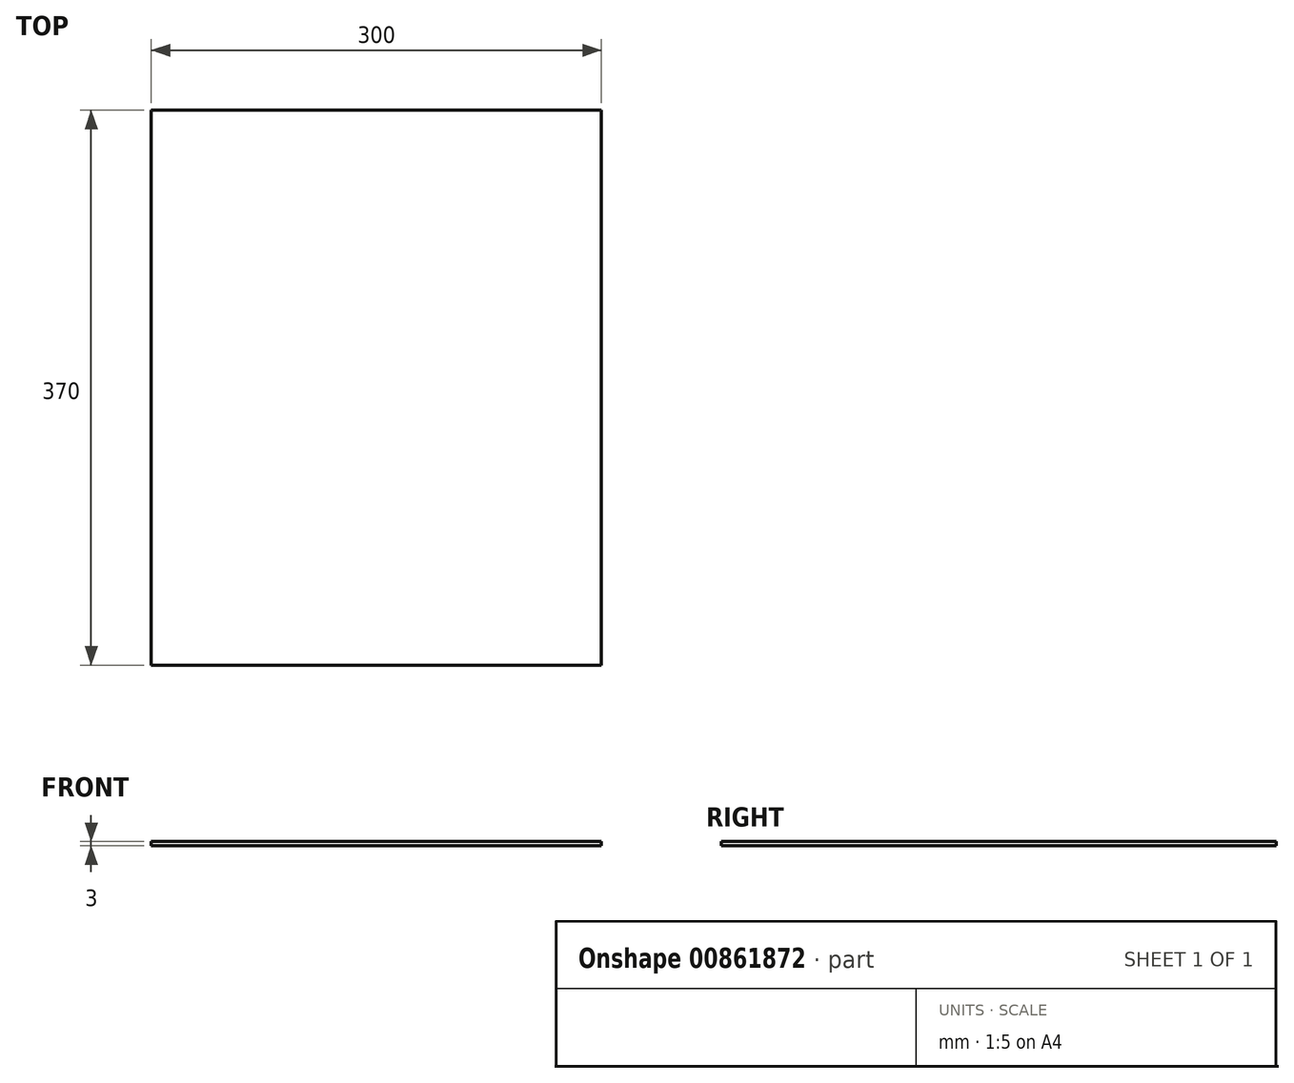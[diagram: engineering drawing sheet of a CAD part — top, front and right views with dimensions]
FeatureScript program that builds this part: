
annotation { "Feature Type Name" : "Feature", "Feature Type Description" : "" }
export const myFeature = defineFeature(function(context is Context, id is Id, definition is map)
    precondition{}
    {
        {
            var Q0;
            Q0=qCreatedBy(makeId("Top.planeOp"),FACE);
            var sketch = newSketch(context, id + "F0", { "sketchPlane" : qUnion([Q0])});
            skLineSegment(sketch, "E0.bottom", {"start": v(150, -185) * mm, "end": v(-150, -185) * mm});
            skLineSegment(sketch, "E0.top", {"start": v(150, 185) * mm, "end": v(-150, 185) * mm});
            skLineSegment(sketch, "E0.left", {"start": v(150, -185) * mm, "end": v(150, 185) * mm});
            skLineSegment(sketch, "E0.right", {"start": v(-150, -185) * mm, "end": v(-150, 185) * mm});
            skPoint(sketch, "E0.middle", {"position": v(0, 0) * mm});
            skSolve(sketch);
        }
        {
            var Q0;
            Q0 = qSketchRegion(id + "F0", true);
            extrude(context, id + "F1", {"entities" : qUnion([Q0]), "depth" : 3 * mm, "offsetDistance" : 25 * mm});
        }
    });
